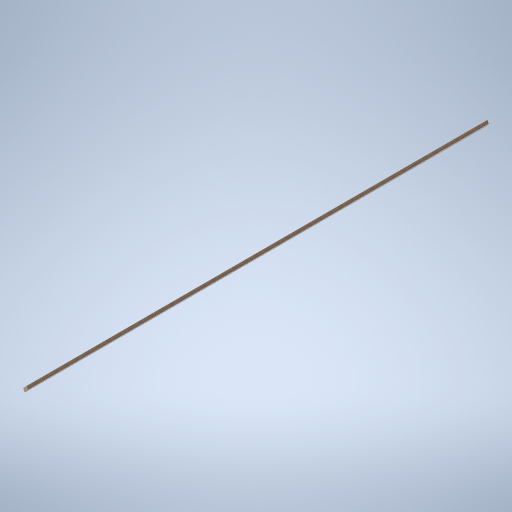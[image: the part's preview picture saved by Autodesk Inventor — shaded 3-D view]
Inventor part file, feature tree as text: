
AUTODESK INVENTOR PART (.ipt)
format: ipt  version: 2024.2 (Build 282272000, 272)  size: 273,920 bytes
history: native  units: mm
features: extrude x1, fillet x1, sketch x1
ambient origin geometry x8: Origin, YZ Plane, XZ Plane, XY Plane, X Axis, Y Axis, Z Axis, Center Point
bodies: Body1 (feature_tree)
feature tree (3):
  extrude  "Extrusion3"  Depth=800.0mm
  fillet  "Fillet2"  Radius=20000.0mm
  sketch  "Sketch2"  dims[d5=8500.0mm d20=800.0mm d21=20000.0mm d22=20000.0mm d23=0.0mm d24=0.0mm d25=50.0mm]
